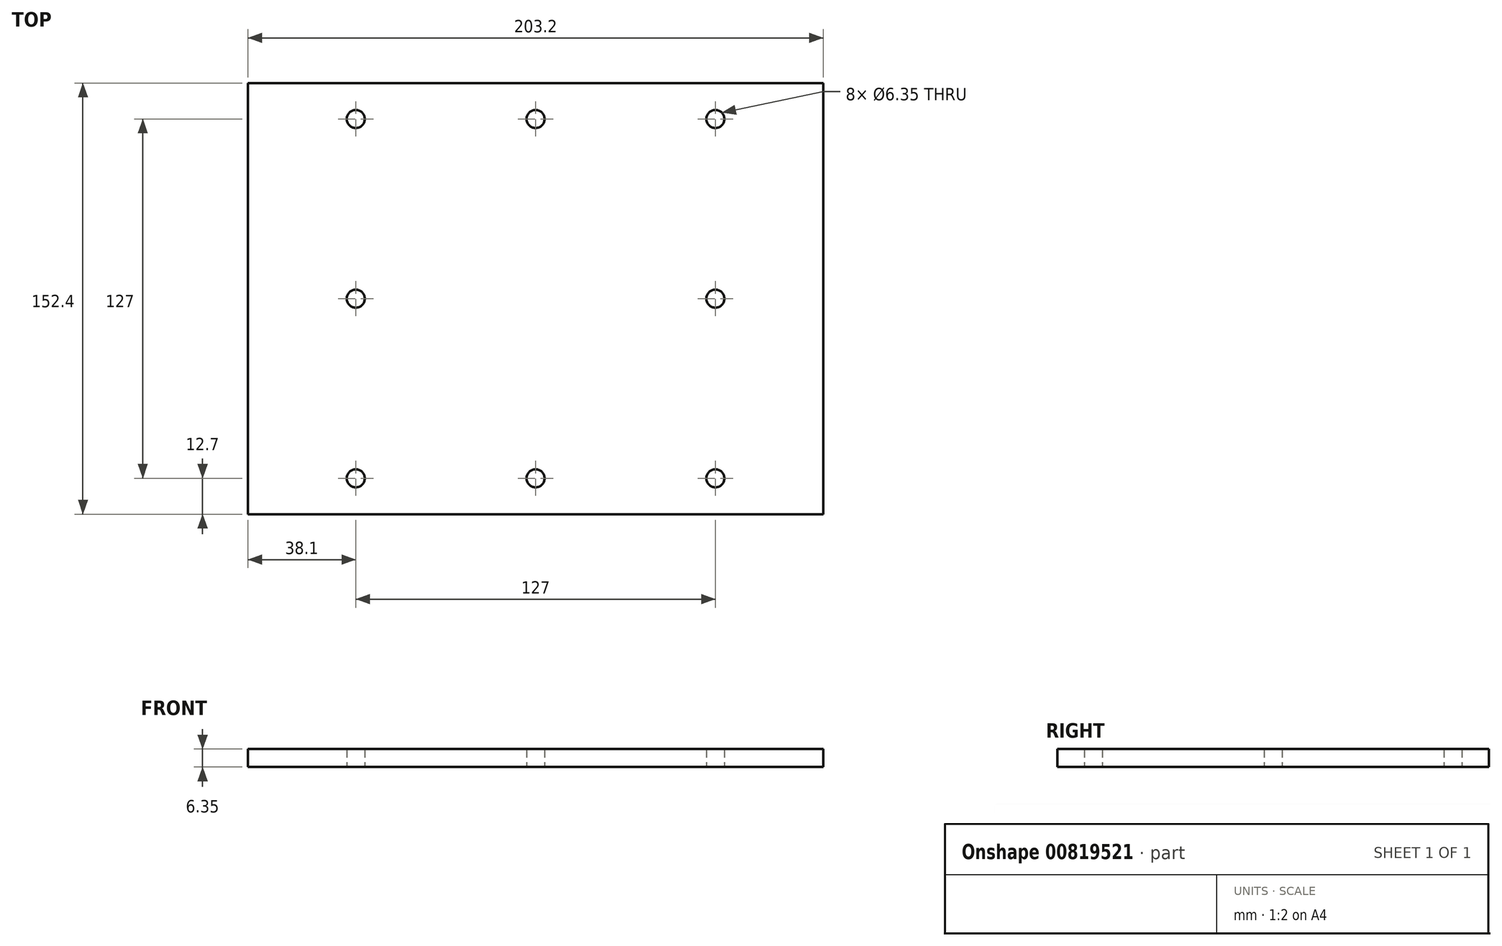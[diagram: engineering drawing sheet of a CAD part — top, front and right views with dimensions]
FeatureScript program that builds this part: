
annotation { "Feature Type Name" : "Feature", "Feature Type Description" : "" }
export const myFeature = defineFeature(function(context is Context, id is Id, definition is map)
    precondition{}
    {
        {
            var Q0;
            Q0=qCreatedBy(makeId("Top.planeOp"),FACE);
            var sketch = newSketch(context, id + "F0", { "sketchPlane" : qUnion([Q0])});
            skLineSegment(sketch, "E0.bottom", {"start": v(-101.6, 76.2) * mm, "end": v(101.6, 76.2) * mm});
            skLineSegment(sketch, "E0.top", {"start": v(-101.6, -76.2) * mm, "end": v(101.6, -76.2) * mm});
            skLineSegment(sketch, "E0.left", {"start": v(-101.6, 76.2) * mm, "end": v(-101.6, -76.2) * mm});
            skLineSegment(sketch, "E0.right", {"start": v(101.6, 76.2) * mm, "end": v(101.6, -76.2) * mm});
            skLineSegment(sketch, "E1.bottom", {"start": v(-63.5, 63.5) * mm, "end": v(63.5, 63.5) * mm, "construction": true});
            skLineSegment(sketch, "E1.top", {"start": v(-63.5, -63.5) * mm, "end": v(63.5, -63.5) * mm, "construction": true});
            skLineSegment(sketch, "E1.left", {"start": v(-63.5, 63.5) * mm, "end": v(-63.5, -63.5) * mm, "construction": true});
            skLineSegment(sketch, "E1.right", {"start": v(63.5, 63.5) * mm, "end": v(63.5, -63.5) * mm, "construction": true});
            skLineSegment(sketch, "E2", {"start": v(-101.6, 0) * mm, "end": v(101.6, 0) * mm, "construction": true});
            skLineSegment(sketch, "E3", {"start": v(0, 76.2) * mm, "end": v(0, -76.2) * mm, "construction": true});
            skCircle(sketch, "E4", {"center": v(-63.5, 63.5) * mm, "radius": 3.18 * mm});
            skCircle(sketch, "E5", {"center": v(63.5, 63.5) * mm, "radius": 3.18 * mm});
            skCircle(sketch, "E6", {"center": v(63.5, 0) * mm, "radius": 3.18 * mm});
            skCircle(sketch, "E7", {"center": v(63.5, -63.5) * mm, "radius": 3.18 * mm});
            skCircle(sketch, "E8", {"center": v(-63.5, 0) * mm, "radius": 3.18 * mm});
            skCircle(sketch, "E9", {"center": v(-63.5, -63.5) * mm, "radius": 3.18 * mm});
            skCircle(sketch, "E10", {"center": v(0, -63.5) * mm, "radius": 3.18 * mm});
            skCircle(sketch, "E11", {"center": v(0, 63.5) * mm, "radius": 3.18 * mm});
            skSolve(sketch);
        }
        {
            var Q0;
            Q0=makeQuery(id+"F0.imprint","IMPRINT",FACE,{"disambiguationData":[TD([[makeQuery(id+"F0.imprint","IMPRINT",EDGE,{"derivedFrom":sQuery(id+"F0.wireOp",EDGE,"E0.bottom")}),-1.0]])]});
            extrude(context, id + "F1", {"entities" : qUnion([Q0]), "depth" : 6.35 * mm, "offsetDistance" : 25.4 * mm});
        }
    });
